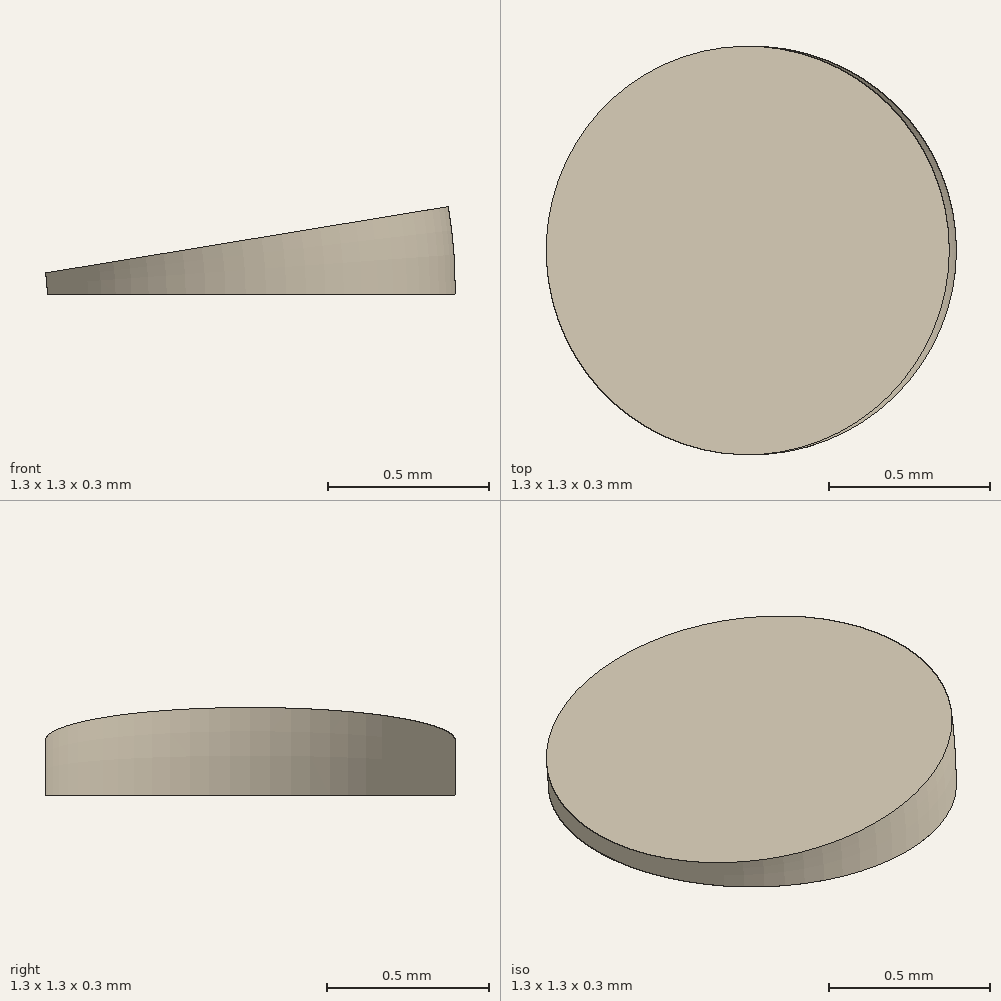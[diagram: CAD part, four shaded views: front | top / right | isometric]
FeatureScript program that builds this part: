
annotation { "Feature Type Name" : "Feature", "Feature Type Description" : "" }
export const myFeature = defineFeature(function(context is Context, id is Id, definition is map)
    precondition{}
    {
        {
            var Q0;
            Q0=qCreatedBy(makeId("Top.planeOp"),FACE);
            var sketch = newSketch(context, id + "F0", { "sketchPlane" : qUnion([Q0])});
            skCircle(sketch, "E0", {"center": v(0, 0) * mm, "radius": 0.64 * mm});
            skSolve(sketch);
        }
        {
            var Q0;
            Q0=qCreatedBy(makeId("Front.planeOp"),FACE);
            var sketch = newSketch(context, id + "F1", { "sketchPlane" : qUnion([Q0])});
            skArc(sketch, "E1", {"start": v(0, 0) * mm, "mid": v(0, 0.08) * mm, "end": v(-0.01, 0.17) * mm});
            skSolve(sketch);
        }
        {
            var Q0;
            Q0=makeQuery(id+"F0.imprint","IMPRINT",FACE,{"disambiguationData":[TD([[makeQuery(id+"F0.imprint","IMPRINT",EDGE,{"derivedFrom":sQuery(id+"F0.wireOp",EDGE,"E0")}),1.0]])]});
            var Q1;
            Q1=sQuery(id+"F1.wireOp",EDGE,"E1");
            sweep(context, id + "F2", {"profiles" : qUnion([Q0]), "path" : qUnion([Q1])});
        }
    });
